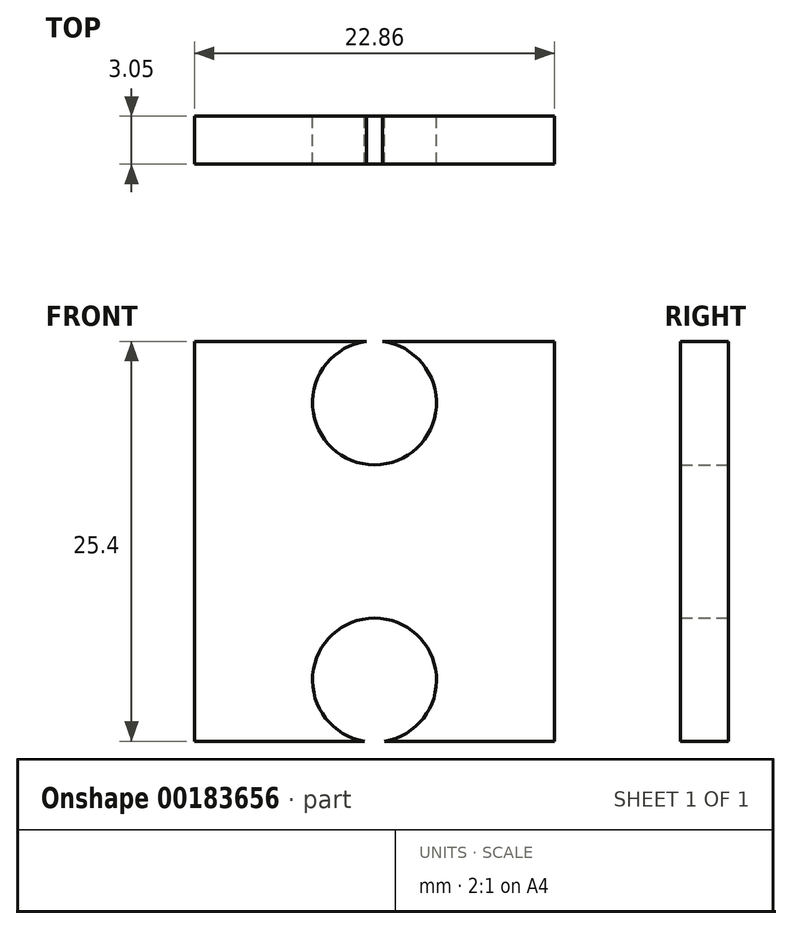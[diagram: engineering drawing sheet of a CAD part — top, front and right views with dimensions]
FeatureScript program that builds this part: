
annotation { "Feature Type Name" : "Feature", "Feature Type Description" : "" }
export const myFeature = defineFeature(function(context is Context, id is Id, definition is map)
    precondition{}
    {
        {
            var Q0;
            Q0=qCreatedBy(makeId("Front.planeOp"),FACE);
            var sketch = newSketch(context, id + "F0", { "sketchPlane" : qUnion([Q0])});
            skLineSegment(sketch, "E0.bottom", {"start": v(11.43, 12.7) * mm, "end": v(-11.43, 12.7) * mm});
            skLineSegment(sketch, "E0.top", {"start": v(11.43, -12.7) * mm, "end": v(-11.43, -12.7) * mm});
            skLineSegment(sketch, "E0.left", {"start": v(11.43, 12.7) * mm, "end": v(11.43, -12.7) * mm});
            skLineSegment(sketch, "E0.right", {"start": v(-11.43, 12.7) * mm, "end": v(-11.43, -12.7) * mm});
            skPoint(sketch, "E0.middle", {"position": v(0, 0) * mm});
            skCircle(sketch, "E1", {"center": v(0, -8.82) * mm, "radius": 3.94 * mm});
            skCircle(sketch, "E2", {"center": v(0, 8.8) * mm, "radius": 3.94 * mm});
            skSolve(sketch);
        }
        {
            var Q0;
            {var subQ4=sQuery(id+"F0.wireOp",EDGE,"E0.left");Q0=makeQuery(id+"F0.imprint","IMPRINT",FACE,{"disambiguationData":[TD([[makeQuery(id+"F0.imprint","IMPRINT",EDGE,{"derivedFrom":subQ4}),-1.0]])]});}
            extrude(context, id + "F1", {"entities" : qUnion([Q0]), "depth" : 3.05 * mm});
        }
    });
